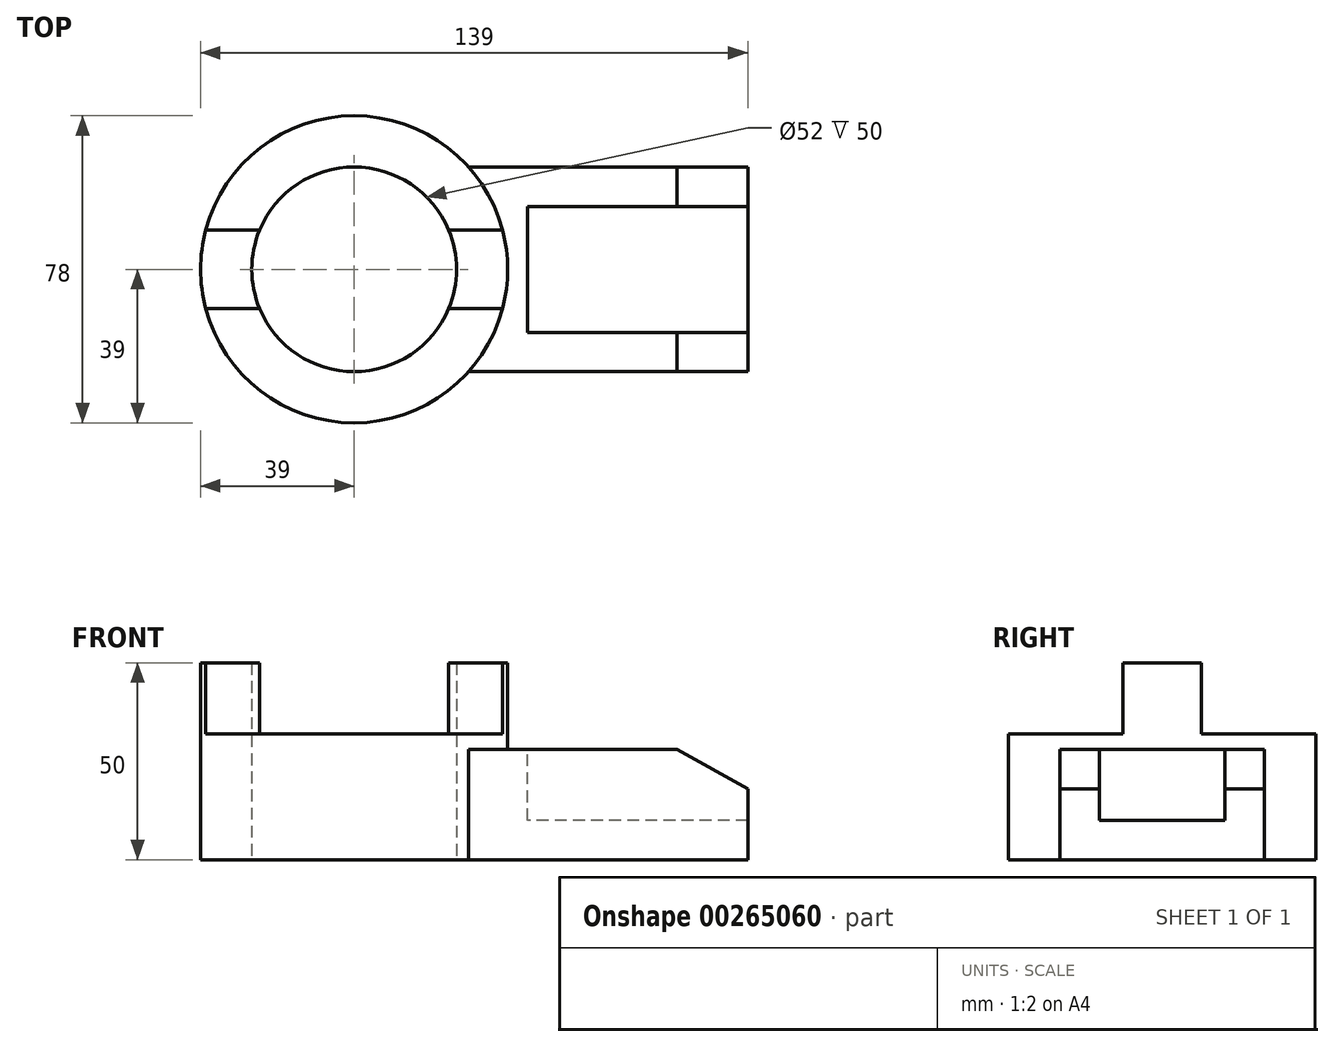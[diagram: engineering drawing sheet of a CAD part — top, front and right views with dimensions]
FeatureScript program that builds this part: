
annotation { "Feature Type Name" : "Feature", "Feature Type Description" : "" }
export const myFeature = defineFeature(function(context is Context, id is Id, definition is map)
    precondition{}
    {
        {
            var Q0;
            Q0=qCreatedBy(makeId("Top.planeOp"),FACE);
            var sketch = newSketch(context, id + "F0", { "sketchPlane" : qUnion([Q0])});
            skCircle(sketch, "E0", {"center": v(0, 0) * mm, "radius": 39 * mm});
            skCircle(sketch, "E1", {"center": v(0, 0) * mm, "radius": 26 * mm});
            skLineSegment(sketch, "E2", {"start": v(29.07, -26) * mm, "end": v(100, -26) * mm});
            skLineSegment(sketch, "E3", {"start": v(100, -26) * mm, "end": v(100, 0) * mm});
            skLineSegment(sketch, "E4.MirrorCS", {"start": v(29.07, 26) * mm, "end": v(100, 26) * mm});
            skLineSegment(sketch, "E5.MirrorCS", {"start": v(100, 26) * mm, "end": v(100, 0) * mm});
            skSolve(sketch);
        }
        {
            var Q0;
            {var subQ1=sQuery(id+"F0.wireOp",EDGE,"E2");Q0=makeQuery(id+"F0.imprint","IMPRINT",FACE,{"disambiguationData":[TD([[makeQuery(id+"F0.imprint","IMPRINT",EDGE,{"derivedFrom":subQ1}),1.0]])]});}
            extrude(context, id + "F1", {"entities" : qUnion([Q0]), "depth" : 28 * mm});
        }
        {
            var Q0;
            Q0=makeQuery(id+"F0.imprint","IMPRINT",FACE,{"disambiguationData":[TD([[makeQuery(id+"F0.imprint","IMPRINT",EDGE,{"derivedFrom":sQuery(id+"F0.wireOp",EDGE,"E1")}),-1.0]])]});
            extrude(context, id + "F2", {"entities" : qUnion([Q0]), "operationType" : NewBodyOperationType.ADD, "depth" : 32 * mm});
        }
        {
            var Q0;
            Q0=makeQuery(id+"F2.opExtrude","CAP_FACE",FACE,{"disambiguationData":[OSD([sQuery(id+"F0.wireOp",EDGE,"E0"),sQuery(id+"F0.wireOp",EDGE,"E1")])],"isStart":false});
            var sketch = newSketch(context, id + "F3", { "sketchPlane" : qUnion([Q0])});
            skArc(sketch, "E6", {"start": v(24, 10) * mm, "mid": v(26, 0) * mm, "end": v(24, -10) * mm});
            skArc(sketch, "E7", {"start": v(37.7, 10) * mm, "mid": v(39, 0) * mm, "end": v(37.7, -10) * mm});
            skLineSegment(sketch, "E8", {"start": v(37.7, -10) * mm, "end": v(24, -10) * mm});
            skLineSegment(sketch, "E9", {"start": v(37.7, 10) * mm, "end": v(24, 10) * mm});
            skLineSegment(sketch, "E10.MirrorCS", {"start": v(-37.7, 10) * mm, "end": v(-24, 10) * mm});
            skArc(sketch, "E11.MirrorCS", {"start": v(-24, 10) * mm, "mid": v(-26, 0) * mm, "end": v(-24, -10) * mm});
            skArc(sketch, "E12.MirrorCS", {"start": v(-37.7, 10) * mm, "mid": v(-39, 0) * mm, "end": v(-37.7, -10) * mm});
            skLineSegment(sketch, "E13.MirrorCS", {"start": v(-37.7, -10) * mm, "end": v(-24, -10) * mm});
            skSolve(sketch);
        }
        {
            var Q0;
            Q0=makeQuery(id+"F3.imprint","IMPRINT",FACE,{"disambiguationData":[TD([[makeQuery(id+"F3.imprint","IMPRINT",EDGE,{"derivedFrom":sQuery(id+"F3.wireOp",EDGE,"E6")}),-1.0]])]});
            var Q1;
            Q1=makeQuery(id+"F3.imprint","IMPRINT",FACE,{"disambiguationData":[TD([[makeQuery(id+"F3.imprint","IMPRINT",EDGE,{"derivedFrom":sQuery(id+"F3.wireOp",EDGE,"E10.MirrorCS")}),-1.0]])]});
            extrude(context, id + "F4", {"entities" : qUnion([Q0, Q1]), "operationType" : NewBodyOperationType.ADD, "depth" : 18 * mm});
        }
        {
            var Q0;
            Q0=makeQuery(id+"F1.opExtrude","CAP_FACE",FACE,{"disambiguationData":[OSD([sQuery(id+"F0.wireOp",EDGE,"E0"),sQuery(id+"F0.wireOp",EDGE,"E2"),sQuery(id+"F0.wireOp",EDGE,"E3"),sQuery(id+"F0.wireOp",EDGE,"E4.MirrorCS"),sQuery(id+"F0.wireOp",EDGE,"E5.MirrorCS")])],"isStart":false});
            var sketch = newSketch(context, id + "F5", { "sketchPlane" : qUnion([Q0])});
            skLineSegment(sketch, "E14", {"start": v(100, 0) * mm, "end": v(100, -16) * mm});
            skLineSegment(sketch, "E15", {"start": v(100, -16) * mm, "end": v(44, -16) * mm});
            skLineSegment(sketch, "E16", {"start": v(44, -16) * mm, "end": v(44, 16) * mm});
            skLineSegment(sketch, "E17", {"start": v(44, 16) * mm, "end": v(100, 16) * mm});
            skSolve(sketch);
        }
        {
            var Q0;
            {var subQ1=sQuery(id+"F5.wireOp",EDGE,"E14");Q0=makeQuery(id+"F5.imprint","IMPRINT",FACE,{"disambiguationData":[TD([[makeQuery(id+"F5.imprint","IMPRINT",EDGE,{"derivedFrom":subQ1}),1.0]])]});}
            extrude(context, id + "F6", {"entities" : qUnion([Q0]), "operationType" : NewBodyOperationType.REMOVE, "oppositeDirection" : true, "depth" : 18 * mm});
        }
        {
            var Q0;
            Q0=makeQuery(id+"F1.opExtrude","SWEPT_FACE",FACE,{"disambiguationData":[OSD([sQuery(id+"F0.wireOp",EDGE,"E2")])]});
            var sketch = newSketch(context, id + "F7", { "sketchPlane" : qUnion([Q0])});
            skLineSegment(sketch, "E18", {"start": v(100, 28) * mm, "end": v(100, 18) * mm});
            skLineSegment(sketch, "E19", {"start": v(100, 18) * mm, "end": v(82, 28) * mm});
            skLineSegment(sketch, "E20", {"start": v(82, 28) * mm, "end": v(100, 28) * mm});
            skSolve(sketch);
        }
        {
            var Q0;
            Q0=makeQuery(id+"F7.imprint","IMPRINT",FACE,{"disambiguationData":[TD([[makeQuery(id+"F7.imprint","IMPRINT",EDGE,{"derivedFrom":sQuery(id+"F7.wireOp",EDGE,"E18")}),-1.0]])]});
            extrude(context, id + "F8", {"entities" : qUnion([Q0]), "operationType" : NewBodyOperationType.REMOVE, "oppositeDirection" : true, "depth" : 100 * mm});
        }
    });
